# Revit family: Legrand_ElectricFireStopping_EZPathFirestopModule_Series44_Floor
name_source: partatom
category: Equipement spécialisé
units: mm (PartAtom-declared; Revit-internal decimal feet)

## family parameters
Cote de connecteur circulaire = Utiliser le diamètre
Couper avec des vides une fois chargée = Non
Hôte = Sol
Numéro OmniClass = 23.20.50.14
Partagée = Non
Point de calcul de pièce = Non
Titre OmniClass = Firestopping
Toujours verticalement = Oui
Type d'élément = Normal

## types (8) — shared parameters
AirLeakage(UL1479) = 1.57 m3/h 0% cable, 3.24 m3/h 100% cable
AssetType = Fixed
Base Plate Filler Plate 2 = Non
Base Plate Filler Plate 3 = Non
BasePlateCutoutCenterlineLength = 58.7375 mm  [stored 0.192708 ft]
BasePlateCutoutLength = 117.475 mm  [stored 0.385417 ft]
Classification(EN13501-2) = EI 120
ClassificationName = Uniclass2015
ClassificationValue = Ss_25_60_30
Code d'assemblage = D4030900
CodePerformance = Conforms to the European standard EN1366-3, BS476/20, ASTM E814 and DIN4102-9
Color = Red
Description = EZ-Path is a mechanical device that provides fully compliant fire stopping for power and data cable management pathways.
DocumentationInstallationGuide = https://www.legrand.co.uk
DocumentationLiterature = https://specifi.bimstore.co.uk
DocumentationTechnical = https://www.legrand.co.uk
DurationUnit = Years
EZPathDevice = Firestop-STI-EZ_Path-Series_44+_Fire_Rated_Pathway
EZPathHeight = 117.475 mm  [stored 0.385417 ft]
EZPathLoadingHeight = 85.725 mm
EZPathLoadingWidth = 95.25 mm  [stored 0.3125 ft]
EZPathOal = 355.6 mm  [stored 1.16667 ft]
EZPathWidth = 101.6 mm
ExpansionBegins = 177 deg C
Fabricant = Legrand Electric Ltd
Features = The modules, which are suitable for all types of wall, can be assembled and installed horizontally or vertically to form a sturdy unit
Finish = Powder Coated
FireRating = Up to 4 Hr
FireResistance(EN1366-3) = 2 Hours
FloorHeightOpening = 117.475 mm  [stored 0.385417 ft]
General Conditions of Use = https://export.legrand.com
IfcExportAs = IfcBuildingElementPart
IfcExportType = IfcBuildingElementPartTypeEnum.FIRESTOP
InServiceTemperature = Not to exceed 49 deg C
ManufacturerName = Legrand Electric Ltd
Material = 1.5mm thk Galv Steel
ModelNumber = CM250058
ModelNumberDevice = CM250058
ModelNumberExtensions = CM250178
ModelReference = EZ-Path® Permanent Automatic Mechanical Firestop System (Series 44) Floor
Modèle = EZ-Path® Permanent Automatic Mechanical Firestop System (Series 44) Floor
NBSDescription = Fire stopping systems
NBSObjectName = Legrand Electric Ltd - Fire Stopping
NBSReference = 30-85-30
NominalHeight = 117.475 mm  [stored 0.385417 ft]
NominalLength = 355.6 mm  [stored 1.16667 ft]
Note d'identification = P12
ProductPage = https://www.legrand.co.uk
ProductionYear = 2017
ReactionToFire(EN13501-1) = Class E
ReferencedStandard = CE Marking, EN 1366-3, ETA 130993
Region = Europe
RetainingPlate = Firestop-STI-EZ_Path-Retaining_Plate
SafetyDataSheet = https://files.stifirestop.com
SecondaryModelNumberDevice = EZD44T
SecondaryModelNumberExtensions = EZD44E
Shape = Rectangle (Series 44)
ShelfLife = No Limit
SoundInsulation(ASTME90) = STC 54
TestedSystems = https://www.legrand.co.uk
URL = https://www.legrand.co.uk
VolumeExpansion = 800%
WarrantyDescription = Firestop certification guaranteed throughout the entire lifetime of the electrical installation
WarrantyDurationLabor = 0
WarrantyDurationParts = 0
WarrantyDurationUnit = Years
Weight(Kg) = 2.67 kg
_BSBibleVersion = 15
_CurrentRevision = 2
_DistributedBy = www.bimstore.co.uk
group 1 device 1 = Oui
group 3 Upper Plate = Non
group 3 device 1 = Non
group 3 device 2 = Non
group 3 device 3 = Non
group 3 device 4 = Non
group 4 Upper Plate = Non
group 4 device 1 = Non
group 4 device 2 = Non
group 4 device 3 = Non
group 4 device 4 = Non
zero-valued in all types: BasePlateFillerPlateCenterlineLength1, BasePlateFillerPlateCenterlineLength2, BasePlateFillerPlateCenterlineLength3, BasePlateFillerPlateCenterlineWidth1, BasePlateFillerPlateCenterlineWidth2, BasePlateFillerPlateCenterlineWidth3, EZPathHeightCenterlineGroup1, EZPathHeightCenterlineGroup2, EZPathWidthCenterlineGroup3, EZPathWidthCenterlineGroup4, Elévation par défaut, ExpectedLife, NoOfExtensions, _BimSpecGuid, group 3 device No, group 4 device No

## per-type parameters (varying)
- 5 Devices Cast In Place (Concrete Floors Only) (Series 44) Réf 5 x 250058 + 350704: BIMObjectName=Legrand_ElectricFireStopping_EZPathFirestopModule_Series44_Floor_5DeviceCastInPlace; Base Plate=Non; Base Plate Filler Plate 1=Non; Base Plate Filler Plate No=0; Base Plate ON OFF=0; BasePlateAboveFloor=6.35 mm  [stored 0.0208333 ft]; BasePlateCenterlineLength=136.525 mm  [stored 0.447917 ft]; BasePlateFillerPlateLength=31.75 mm  [stored 0.104167 ft]; BasePlateFillerPlateWidth=406.4 mm  [stored 1.33333 ft]; BasePlateLength=273.05 mm  [stored 0.895833 ft]; BasePlateWidth=263.525 mm; BasePlateWidthCutout=101.6 mm; Commentaires du type=5 Devices Cast In Place (Concrete Floors Only) (Series 44); EZPathAboveFloor=50.00625 mm  [stored 0.164062 ft]; EZPathHeightCenterlineGroup3=0 mm  [stored 0 ft]; EZPathHeightCenterlineGroup4=0 mm  [stored 0 ft]; EZPathWidthCenterlineGroup1=50.8 mm; EZPathWidthCenterlineGroup2=152.4 mm  [stored 0.5 ft]; FloorWidthOpening=508 mm; ModelNumberBrackets=CM350704; NoOfDevices=5; NominalWidth=508 mm; SecondaryModelNumberBrackets=EZP544MBE; Size=117x508mm; TypeName=5 Devices Cast In Place (Concrete Floors Only) (Series 44); Upper Plate No=0; UpperPlateAboveLowerPlate=41.275 mm; UpperPlateBackFlangeThk=1.5875 mm  [stored 0.00520833 ft]; UpperPlateBackPlateWidth=104.775 mm  [stored 0.34375 ft]; UpperPlateBackPlateWidthBank1=127 mm  [stored 0.416667 ft]; UpperPlateBackPlateWidthBank1Centerline=12.7 mm  [stored 0.0416667 ft]; UpperPlateBackWidthThk=127 mm  [stored 0.416667 ft]; UpperPlateBackWidthThkBank1=104.775 mm  [stored 0.34375 ft]; UpperPlateBackWidthThkBank1Centerline=1.5875 mm  [stored 0.00520833 ft]; UpperPlateFlangeThk=1.5875 mm  [stored 0.00520833 ft]; UpperPlateWidth=101.6 mm; UpperPlateWidthBank1=101.6 mm; UpperPlateWidthBank1Centerline=0 mm  [stored 0 ft]; group 1 Upper Plate=Non; group 1 device 2=Oui; group 1 device 3=Oui; group 1 device 4=Oui; group 1 device No=4; group 2 Upper Plate=Non; group 2 device 1=Oui; group 2 device 2=Non; group 2 device 3=Non; group 2 device 4=Non; group 2 device No=1
- 4 Devices Cast In Place (Concrete Floors Only) (Series 44) Réf 4 x 250058 + 350704: BIMObjectName=Legrand_ElectricFireStopping_EZPathFirestopModule_Series44_Floor_4DeviceCastInPlace; Base Plate=Non; Base Plate Filler Plate 1=Non; Base Plate Filler Plate No=0; Base Plate ON OFF=0; BasePlateAboveFloor=6.35 mm  [stored 0.0208333 ft]; BasePlateCenterlineLength=136.525 mm  [stored 0.447917 ft]; BasePlateFillerPlateLength=31.75 mm  [stored 0.104167 ft]; BasePlateFillerPlateWidth=406.4 mm  [stored 1.33333 ft]; BasePlateLength=273.05 mm  [stored 0.895833 ft]; BasePlateWidth=263.525 mm; BasePlateWidthCutout=101.6 mm; Commentaires du type=4 Devices Cast In Place (Concrete Floors Only) (Series 44); EZPathAboveFloor=50.00625 mm  [stored 0.164062 ft]; EZPathHeightCenterlineGroup3=0 mm  [stored 0 ft]; EZPathHeightCenterlineGroup4=0 mm  [stored 0 ft]; EZPathWidthCenterlineGroup1=0 mm  [stored 0 ft]; EZPathWidthCenterlineGroup2=0 mm  [stored 0 ft]; FloorWidthOpening=406.4 mm  [stored 1.33333 ft]; ModelNumberBrackets=CM350704; NoOfDevices=4; NominalWidth=406.4 mm  [stored 1.33333 ft]; SecondaryModelNumberBrackets=EZP544MBE; Size=117x406mm; TypeName=4 Devices Cast In Place (Concrete Floors Only) (Series 44); Upper Plate No=0; UpperPlateAboveLowerPlate=41.275 mm; UpperPlateBackFlangeThk=1.5875 mm  [stored 0.00520833 ft]; UpperPlateBackPlateWidth=104.775 mm  [stored 0.34375 ft]; UpperPlateBackPlateWidthBank1=127 mm  [stored 0.416667 ft]; UpperPlateBackPlateWidthBank1Centerline=12.7 mm  [stored 0.0416667 ft]; UpperPlateBackWidthThk=127 mm  [stored 0.416667 ft]; UpperPlateBackWidthThkBank1=104.775 mm  [stored 0.34375 ft]; UpperPlateBackWidthThkBank1Centerline=1.5875 mm  [stored 0.00520833 ft]; UpperPlateFlangeThk=1.5875 mm  [stored 0.00520833 ft]; UpperPlateWidth=101.6 mm; UpperPlateWidthBank1=101.6 mm; UpperPlateWidthBank1Centerline=0 mm  [stored 0 ft]; group 1 Upper Plate=Non; group 1 device 2=Oui; group 1 device 3=Oui; group 1 device 4=Oui; group 1 device No=4; group 2 Upper Plate=Non; group 2 device 1=Non; group 2 device 2=Non; group 2 device 3=Non; group 2 device 4=Non; group 2 device No=0
- 3 Devices Cast In Place (Concrete Floors Only) (Series 44) Réf 3 x 250058 + 350704: BIMObjectName=Legrand_ElectricFireStopping_EZPathFirestopModule_Series44_Floor_3DeviceCastInPlace; Base Plate=Non; Base Plate Filler Plate 1=Non; Base Plate Filler Plate No=0; Base Plate ON OFF=0; BasePlateAboveFloor=6.35 mm  [stored 0.0208333 ft]; BasePlateCenterlineLength=136.525 mm  [stored 0.447917 ft]; BasePlateFillerPlateLength=31.75 mm  [stored 0.104167 ft]; BasePlateFillerPlateWidth=406.4 mm  [stored 1.33333 ft]; BasePlateLength=273.05 mm  [stored 0.895833 ft]; BasePlateWidth=263.525 mm; BasePlateWidthCutout=101.6 mm; Commentaires du type=3 Devices Cast In Place (Concrete Floors Only) (Series 44); EZPathAboveFloor=50.00625 mm  [stored 0.164062 ft]; EZPathHeightCenterlineGroup3=0 mm  [stored 0 ft]; EZPathHeightCenterlineGroup4=0 mm  [stored 0 ft]; EZPathWidthCenterlineGroup1=50.8 mm; EZPathWidthCenterlineGroup2=0 mm  [stored 0 ft]; FloorWidthOpening=304.8 mm  [stored 1 ft]; ModelNumberBrackets=CM350704; NoOfDevices=3; NominalWidth=304.8 mm  [stored 1 ft]; SecondaryModelNumberBrackets=EZP544MBE; Size=117x305mm; TypeName=3 Devices Cast In Place (Concrete Floors Only) (Series 44); Upper Plate No=0; UpperPlateAboveLowerPlate=41.275 mm; UpperPlateBackFlangeThk=1.5875 mm  [stored 0.00520833 ft]; UpperPlateBackPlateWidth=104.775 mm  [stored 0.34375 ft]; UpperPlateBackPlateWidthBank1=127 mm  [stored 0.416667 ft]; UpperPlateBackPlateWidthBank1Centerline=12.7 mm  [stored 0.0416667 ft]; UpperPlateBackWidthThk=127 mm  [stored 0.416667 ft]; UpperPlateBackWidthThkBank1=104.775 mm  [stored 0.34375 ft]; UpperPlateBackWidthThkBank1Centerline=1.5875 mm  [stored 0.00520833 ft]; UpperPlateFlangeThk=1.5875 mm  [stored 0.00520833 ft]; UpperPlateWidth=101.6 mm; UpperPlateWidthBank1=101.6 mm; UpperPlateWidthBank1Centerline=0 mm  [stored 0 ft]; group 1 Upper Plate=Non; group 1 device 2=Oui; group 1 device 3=Oui; group 1 device 4=Non; group 1 device No=3; group 2 Upper Plate=Non; group 2 device 1=Non; group 2 device 2=Non; group 2 device 3=Non; group 2 device 4=Non; group 2 device No=0
- 2 Devices Cast In Place (Concrete Floors Only) (Series 44) Réf 2 x 250058 + 350704: BIMObjectName=Legrand_ElectricFireStopping_EZPathFirestopModule_Series44_Floor_2DeviceCastInPlace; Base Plate=Non; Base Plate Filler Plate 1=Non; Base Plate Filler Plate No=0; Base Plate ON OFF=0; BasePlateAboveFloor=6.35 mm  [stored 0.0208333 ft]; BasePlateCenterlineLength=136.525 mm  [stored 0.447917 ft]; BasePlateFillerPlateLength=31.75 mm  [stored 0.104167 ft]; BasePlateFillerPlateWidth=406.4 mm  [stored 1.33333 ft]; BasePlateLength=273.05 mm  [stored 0.895833 ft]; BasePlateWidth=263.525 mm; BasePlateWidthCutout=101.6 mm; Commentaires du type=2 Devices Cast In Place (Concrete Floors Only) (Series 44); EZPathAboveFloor=50.00625 mm  [stored 0.164062 ft]; EZPathHeightCenterlineGroup3=0 mm  [stored 0 ft]; EZPathHeightCenterlineGroup4=0 mm  [stored 0 ft]; EZPathWidthCenterlineGroup1=0 mm  [stored 0 ft]; EZPathWidthCenterlineGroup2=0 mm  [stored 0 ft]; FloorWidthOpening=203.2 mm; ModelNumberBrackets=CM350704; NoOfDevices=2; NominalWidth=203.2 mm; SecondaryModelNumberBrackets=EZP544MBE; Size=117x203mm; TypeName=2 Devices Cast In Place (Concrete Floors Only) (Series 44); Upper Plate No=0; UpperPlateAboveLowerPlate=41.275 mm; UpperPlateBackFlangeThk=1.5875 mm  [stored 0.00520833 ft]; UpperPlateBackPlateWidth=104.775 mm  [stored 0.34375 ft]; UpperPlateBackPlateWidthBank1=127 mm  [stored 0.416667 ft]; UpperPlateBackPlateWidthBank1Centerline=12.7 mm  [stored 0.0416667 ft]; UpperPlateBackWidthThk=127 mm  [stored 0.416667 ft]; UpperPlateBackWidthThkBank1=104.775 mm  [stored 0.34375 ft]; UpperPlateBackWidthThkBank1Centerline=1.5875 mm  [stored 0.00520833 ft]; UpperPlateFlangeThk=1.5875 mm  [stored 0.00520833 ft]; UpperPlateWidth=101.6 mm; UpperPlateWidthBank1=101.6 mm; UpperPlateWidthBank1Centerline=0 mm  [stored 0 ft]; group 1 Upper Plate=Non; group 1 device 2=Oui; group 1 device 3=Non; group 1 device 4=Non; group 1 device No=2; group 2 Upper Plate=Non; group 2 device 1=Non; group 2 device 2=Non; group 2 device 3=Non; group 2 device 4=Non; group 2 device No=0
- 2 Bank European Floor Grid – Side by Side (Series 44) Réf 250058 + 250380: BIMObjectName=Legrand_ElectricFireStopping_EZPathFirestopModule_Series44_Floor_2BankGridSideBySide_European; Base Plate=Oui; Base Plate Filler Plate 1=Oui; Base Plate Filler Plate No=1; Base Plate ON OFF=1; BasePlateAboveFloor=11.1125 mm  [stored 0.0364583 ft]; BasePlateCenterlineLength=71.4375 mm; BasePlateFillerPlateLength=117.475 mm  [stored 0.385417 ft]; BasePlateFillerPlateWidth=161.13125 mm; BasePlateLength=210.34375 mm; BasePlateWidth=1135.0625 mm; BasePlateWidthCutout=973.93125 mm; Commentaires du type=2 Bank European Floor Grid – Side by Side (Series 44); EZPathAboveFloor=100.80625 mm  [stored 0.330729 ft]; EZPathHeightCenterlineGroup3=113.109375 mm; EZPathHeightCenterlineGroup4=113.109375 mm; EZPathWidthCenterlineGroup1=283.76562 mm; EZPathWidthCenterlineGroup2=283.76562 mm; FloorWidthOpening=973.93125 mm; ModelNumberBrackets=CM250380; NoOfDevices=8; NominalWidth=973.93125 mm; SecondaryModelNumberBrackets=EZG844T; Size=117x974mm; TypeName=2 Bank European Floor Grid – Side by Side (Series 44); Upper Plate No=2; UpperPlateAboveLowerPlate=32.54375 mm  [stored 0.106771 ft]; UpperPlateBackFlangeThk=32.54375 mm  [stored 0.106771 ft]; UpperPlateBackPlateWidth=479.425 mm  [stored 1.57292 ft]; UpperPlateBackPlateWidthBank1=479.425 mm  [stored 1.57292 ft]; UpperPlateBackPlateWidthBank1Centerline=239.7125 mm  [stored 0.786458 ft]; UpperPlateBackWidthThk=479.425 mm  [stored 1.57292 ft]; UpperPlateBackWidthThkBank1=479.425 mm  [stored 1.57292 ft]; UpperPlateBackWidthThkBank1Centerline=239.7125 mm  [stored 0.786458 ft]; UpperPlateFlangeThk=32.54375 mm  [stored 0.106771 ft]; UpperPlateWidth=406.4 mm  [stored 1.33333 ft]; UpperPlateWidthBank1=406.4 mm  [stored 1.33333 ft]; UpperPlateWidthBank1Centerline=203.2 mm; group 1 Upper Plate=Oui; group 1 device 2=Oui; group 1 device 3=Oui; group 1 device 4=Oui; group 1 device No=4; group 2 Upper Plate=Oui; group 2 device 1=Oui; group 2 device 2=Oui; group 2 device 3=Oui; group 2 device 4=Oui; group 2 device No=4
- 1 Bank European Floor Grid (Series 44) Réf 4 x 250058 + 250370: BIMObjectName=Legrand_ElectricFireStopping_EZPathFirestopModule_Series44_Floor_1BankGrid_European; Base Plate=Oui; Base Plate Filler Plate 1=Non; Base Plate Filler Plate No=0; Base Plate ON OFF=1; BasePlateAboveFloor=11.1125 mm  [stored 0.0364583 ft]; BasePlateCenterlineLength=71.4375 mm; BasePlateFillerPlateLength=31.75 mm  [stored 0.104167 ft]; BasePlateFillerPlateWidth=406.4 mm  [stored 1.33333 ft]; BasePlateLength=210.34375 mm; BasePlateWidth=567.53125 mm; BasePlateWidthCutout=406.4 mm  [stored 1.33333 ft]; Commentaires du type=1 Bank European Floor Grid (Series 44); EZPathAboveFloor=100.80625 mm  [stored 0.330729 ft]; EZPathHeightCenterlineGroup3=0 mm  [stored 0 ft]; EZPathHeightCenterlineGroup4=0 mm  [stored 0 ft]; EZPathWidthCenterlineGroup1=0 mm  [stored 0 ft]; EZPathWidthCenterlineGroup2=0 mm  [stored 0 ft]; FloorWidthOpening=406.4 mm  [stored 1.33333 ft]; ModelNumberBrackets=CM250370; NoOfDevices=4; NominalWidth=406.4 mm  [stored 1.33333 ft]; SecondaryModelNumberBrackets=EZG444T; Size=117x406mm; TypeName=1 Bank European Floor Grid (Series 44); Upper Plate No=1; UpperPlateAboveLowerPlate=32.54375 mm  [stored 0.106771 ft]; UpperPlateBackFlangeThk=32.54375 mm  [stored 0.106771 ft]; UpperPlateBackPlateWidth=479.425 mm  [stored 1.57292 ft]; UpperPlateBackPlateWidthBank1=479.425 mm  [stored 1.57292 ft]; UpperPlateBackPlateWidthBank1Centerline=239.7125 mm  [stored 0.786458 ft]; UpperPlateBackWidthThk=479.425 mm  [stored 1.57292 ft]; UpperPlateBackWidthThkBank1=479.425 mm  [stored 1.57292 ft]; UpperPlateBackWidthThkBank1Centerline=239.7125 mm  [stored 0.786458 ft]; UpperPlateFlangeThk=32.54375 mm  [stored 0.106771 ft]; UpperPlateWidth=406.4 mm  [stored 1.33333 ft]; UpperPlateWidthBank1=406.4 mm  [stored 1.33333 ft]; UpperPlateWidthBank1Centerline=203.2 mm; group 1 Upper Plate=Oui; group 1 device 2=Oui; group 1 device 3=Oui; group 1 device 4=Oui; group 1 device No=4; group 2 Upper Plate=Non; group 2 device 1=Non; group 2 device 2=Non; group 2 device 3=Non; group 2 device 4=Non; group 2 device No=0
- 1 Device European Floor Plate (Series 44) Réf 250058 + 250260: BIMObjectName=Legrand_ElectricFireStopping_EZPathFirestopModule_Series44_Floor_1DeviceFloorPlate_European; Base Plate=Oui; Base Plate Filler Plate 1=Non; Base Plate Filler Plate No=0; Base Plate ON OFF=1; BasePlateAboveFloor=11.1125 mm  [stored 0.0364583 ft]; BasePlateCenterlineLength=136.525 mm  [stored 0.447917 ft]; BasePlateFillerPlateLength=31.75 mm  [stored 0.104167 ft]; BasePlateFillerPlateWidth=406.4 mm  [stored 1.33333 ft]; BasePlateLength=273.05 mm  [stored 0.895833 ft]; BasePlateWidth=263.525 mm; BasePlateWidthCutout=101.6 mm; Commentaires du type=1 Device European Floor Plate (Series 44); EZPathAboveFloor=100.80625 mm  [stored 0.330729 ft]; EZPathHeightCenterlineGroup3=0 mm  [stored 0 ft]; EZPathHeightCenterlineGroup4=0 mm  [stored 0 ft]; EZPathWidthCenterlineGroup1=50.8 mm; EZPathWidthCenterlineGroup2=0 mm  [stored 0 ft]; FloorWidthOpening=101.6 mm; ModelNumberBrackets=CM250260; NoOfDevices=1; NominalWidth=101.6 mm; SecondaryModelNumberBrackets=EZG144T; Size=117x102mm; TypeName=1 Device European Floor Plate (Series 44); Upper Plate No=1; UpperPlateAboveLowerPlate=32.54375 mm  [stored 0.106771 ft]; UpperPlateBackFlangeThk=32.54375 mm  [stored 0.106771 ft]; UpperPlateBackPlateWidth=104.775 mm  [stored 0.34375 ft]; UpperPlateBackPlateWidthBank1=127 mm  [stored 0.416667 ft]; UpperPlateBackPlateWidthBank1Centerline=12.7 mm  [stored 0.0416667 ft]; UpperPlateBackWidthThk=127 mm  [stored 0.416667 ft]; UpperPlateBackWidthThkBank1=127 mm  [stored 0.416667 ft]; UpperPlateBackWidthThkBank1Centerline=12.7 mm  [stored 0.0416667 ft]; UpperPlateFlangeThk=32.54375 mm  [stored 0.106771 ft]; UpperPlateWidth=101.6 mm; UpperPlateWidthBank1=101.6 mm; UpperPlateWidthBank1Centerline=0 mm  [stored 0 ft]; group 1 Upper Plate=Oui; group 1 device 2=Non; group 1 device 3=Non; group 1 device 4=Non; group 1 device No=1; group 2 Upper Plate=Non; group 2 device 1=Non; group 2 device 2=Non; group 2 device 3=Non; group 2 device 4=Non; group 2 device No=0
- 1 Device Cast In Place (Grouted) (Series 44) Réf 250058 + 350703: BIMObjectName=Legrand_ElectricFireStopping_EZPathFirestopModule_Series44_Floor_1DeviceCastInPlace; Base Plate=Non; Base Plate Filler Plate 1=Non; Base Plate Filler Plate No=0; Base Plate ON OFF=0; BasePlateAboveFloor=6.35 mm  [stored 0.0208333 ft]; BasePlateCenterlineLength=136.525 mm  [stored 0.447917 ft]; BasePlateFillerPlateLength=31.75 mm  [stored 0.104167 ft]; BasePlateFillerPlateWidth=406.4 mm  [stored 1.33333 ft]; BasePlateLength=273.05 mm  [stored 0.895833 ft]; BasePlateWidth=263.525 mm; BasePlateWidthCutout=101.6 mm; Commentaires du type=1 Device Cast In Place (Grouted) (Series 44); EZPathAboveFloor=50.00625 mm  [stored 0.164062 ft]; EZPathHeightCenterlineGroup3=0 mm  [stored 0 ft]; EZPathHeightCenterlineGroup4=0 mm  [stored 0 ft]; EZPathWidthCenterlineGroup1=50.8 mm; EZPathWidthCenterlineGroup2=0 mm  [stored 0 ft]; FloorWidthOpening=101.6 mm; ModelNumberBrackets=CM350703; NoOfDevices=1; NominalWidth=101.6 mm; SecondaryModelNumberBrackets=EZP144MBE; Size=117x102mm; TypeName=1 Device Cast In Place (Grouted) (Series 44); Upper Plate No=0; UpperPlateAboveLowerPlate=41.275 mm; UpperPlateBackFlangeThk=1.5875 mm  [stored 0.00520833 ft]; UpperPlateBackPlateWidth=104.775 mm  [stored 0.34375 ft]; UpperPlateBackPlateWidthBank1=127 mm  [stored 0.416667 ft]; UpperPlateBackPlateWidthBank1Centerline=12.7 mm  [stored 0.0416667 ft]; UpperPlateBackWidthThk=127 mm  [stored 0.416667 ft]; UpperPlateBackWidthThkBank1=104.775 mm  [stored 0.34375 ft]; UpperPlateBackWidthThkBank1Centerline=1.5875 mm  [stored 0.00520833 ft]; UpperPlateFlangeThk=1.5875 mm  [stored 0.00520833 ft]; UpperPlateWidth=101.6 mm; UpperPlateWidthBank1=101.6 mm; UpperPlateWidthBank1Centerline=0 mm  [stored 0 ft]; group 1 Upper Plate=Non; group 1 device 2=Non; group 1 device 3=Non; group 1 device 4=Non; group 1 device No=1; group 2 Upper Plate=Non; group 2 device 1=Non; group 2 device 2=Non; group 2 device 3=Non; group 2 device 4=Non; group 2 device No=0

note: [stored X ft] marks values corroborated as IEEE doubles in the binary element streams (Revit-internal decimal feet)

## geometry (parser evidence)
native form markers: Blend x2, Sweep x3
no freeform markers — native parametric forms only
